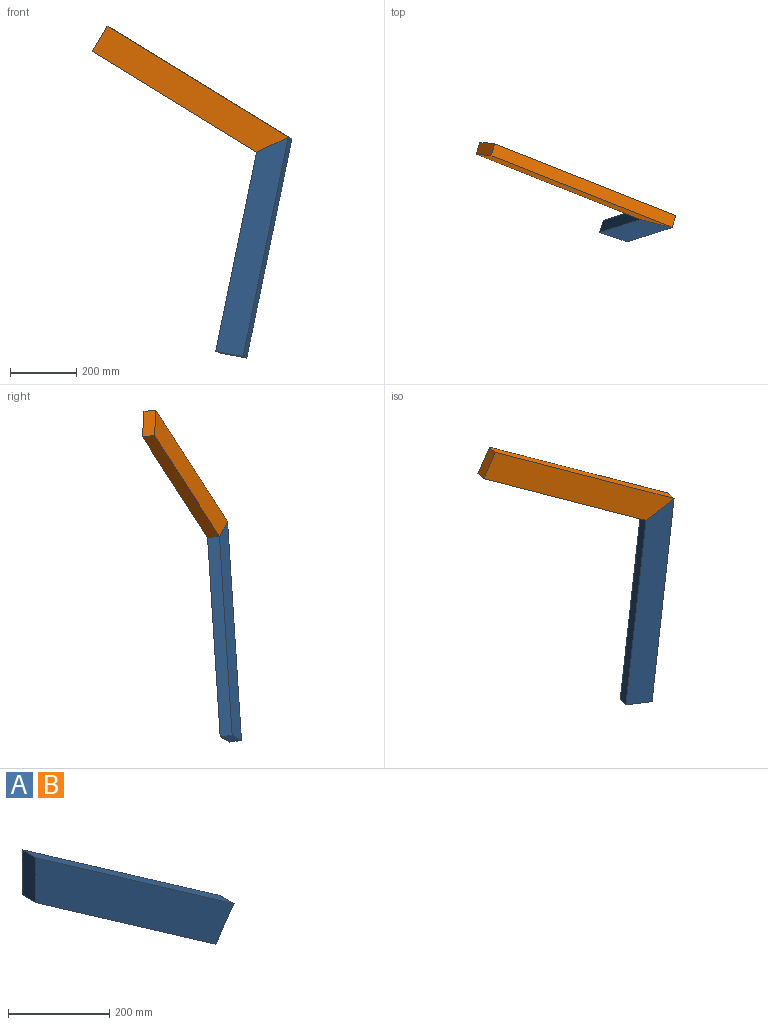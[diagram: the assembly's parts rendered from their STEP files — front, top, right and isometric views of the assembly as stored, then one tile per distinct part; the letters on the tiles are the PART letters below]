
ASSEMBLY  parts=2 mates=1
PART A: 6 faces, bbox 554.5x38.1x461.1 mm
  f0: plane 554.48x388.28mm, normal (0.57,0,0.82), area 25790.3mm2, adj f1,f3,f4,f5
  f1: plane 108.53x38.1mm, normal (-1,0,0), area 4135.2mm2, adj f0,f2,f4,f5
  f2: plane 503.49x352.56mm, normal (-0.57,0,-0.82), area 23418.3mm2, adj f1,f3,f4,f5
  f3: plane 72.82x50.99mm, normal (0.82,0,-0.57), area 3387.1mm2, adj f0,f2,f4,f5
  f4: plane 554.48x461.1mm, normal (0,-1,0), area 57411.4mm2, adj f0,f1,f2,f3
  f5: plane 554.48x461.1mm, normal (0,1,0), area 57411.4mm2, adj f0,f1,f2,f3
PART B: same geometry as A
PLACE A rot(axis=(0.06,0.96,-0.29),68.4deg) t=(520.38,-49.29,155.59)mm
PLACE B rot(axis=(0.54,-0.03,0.84),161.5deg) t=(508.98,-85.34,160.22)mm
MATE fastened A.f1 <-> B.f1  axis (-0.37,0.23,0.9) through (466.96,-55.15,135.1)mm
